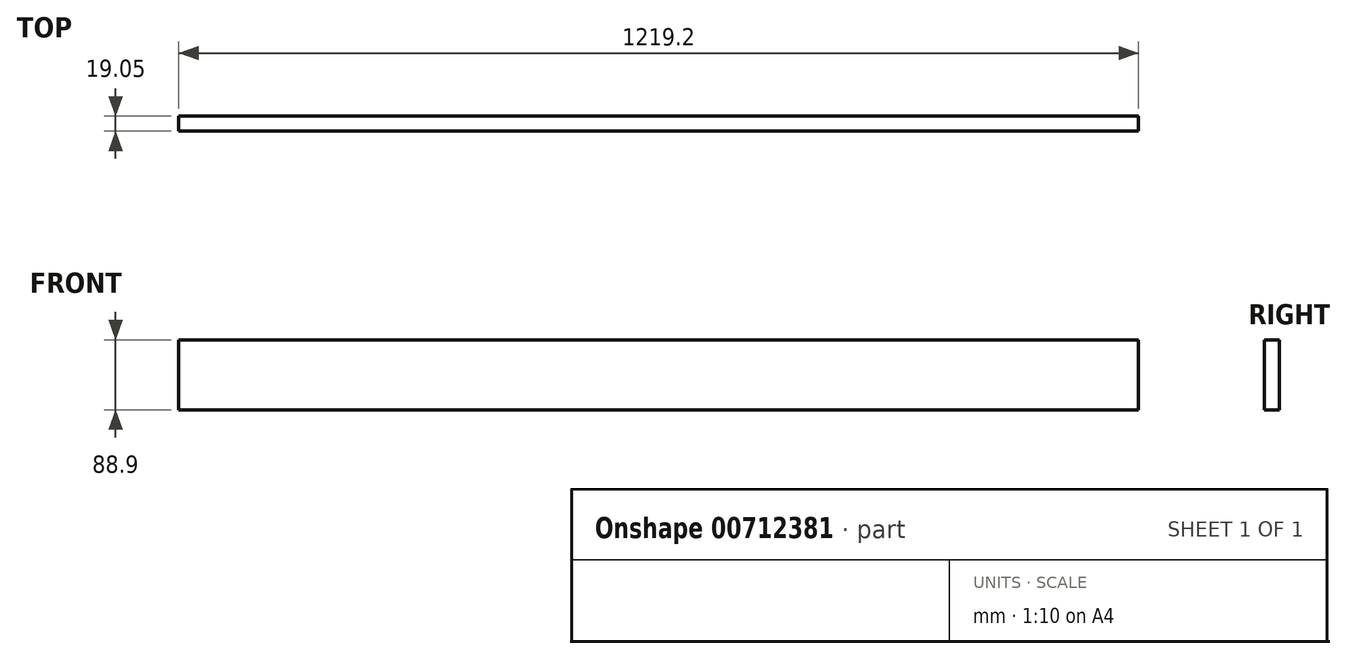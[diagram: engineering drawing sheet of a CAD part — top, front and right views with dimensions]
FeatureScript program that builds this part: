
annotation { "Feature Type Name" : "Feature", "Feature Type Description" : "" }
export const myFeature = defineFeature(function(context is Context, id is Id, definition is map)
    precondition{}
    {
        {
            var Q0;
            Q0=qCreatedBy(makeId("Front.planeOp"),FACE);
            var sketch = newSketch(context, id + "F0", { "sketchPlane" : qUnion([Q0])});
            skLineSegment(sketch, "E0.bottom", {"start": v(0, 0) * mm, "end": v(1219.2, 0) * mm});
            skLineSegment(sketch, "E0.top", {"start": v(0, 88.9) * mm, "end": v(1219.2, 88.9) * mm});
            skLineSegment(sketch, "E0.left", {"start": v(0, 0) * mm, "end": v(0, 88.9) * mm});
            skLineSegment(sketch, "E0.right", {"start": v(1219.2, 0) * mm, "end": v(1219.2, 88.9) * mm});
            skSolve(sketch);
        }
        {
            var Q0;
            Q0=makeQuery(id+"F0.imprint","IMPRINT",FACE,{"disambiguationData":[TD([[makeQuery(id+"F0.imprint","IMPRINT",EDGE,{"derivedFrom":sQuery(id+"F0.wireOp",EDGE,"E0.bottom")}),1.0]])]});
            extrude(context, id + "F1", {"entities" : qUnion([Q0]), "depth" : 19.05 * mm, "offsetDistance" : 25.4 * mm});
        }
    });
